# Revit family: Rohrschelle Maxima PSM, M10-M12, Ø 84-129, o.D
name_source: partatom
category: HLS-Bauteile
revit_build: Autodesk Revit 2017 (Build: 20190507_1515(x64)
units: mm (PartAtom-declared; Revit-internal decimal feet)

## family parameters
Arbeitsebenenbasiert = Ja
Beim Laden mit Abzugskörper schneiden = Nein
Bemaßung runder Anschluss = Durchmesser verwenden
Gemeinsam genutzt = Ja
Immer vertikal = Nein
Raumberechnungspunkt = Nein
Teiletyp = Normal

## types (6) — shared parameters
A = 25 mm  [stored 0.082021 ft]
Anschluss = M10/M12
Anschlußhöhe = 24 mm
Bauart = zweiteilig
Brandschutz = RAL-GZ 656
DF1 = 26 mm
DF2 = 28 mm  [stored 0.0918635 ft]
DVS = 15 mm  [stored 0.0492126 ft]
Fabrikat = MEFA
Firma = MEFA Befestigungs- und Montagesysteme GmbH
HGA = 22 mm  [stored 0.0721785 ft]
Kurztext1 = Rohrschelle Maxima PSM 30x3,0
MB = 30 mm  [stored 0.0984252 ft]
MD = 3 mm  [stored 0.00984252 ft]
Material = Stahl
Materialmaße = 30x3,0 mm
Materialname = S235
Mengeneinheit = St
Oberflaeche = galvanisch verzinkt
Verschluss = Pendelsteckmuttern
Verschluss-Schraube = M8
Vorgabe-Ansicht = 1219 mm
max. zul. Last = 4.00 kN
max. zul. Last horizontal = 0.00 kN
max. zul. Last vertikal = 0.00 kN
vpe = 1 St
zero-valued in all types: Nennweite DN Rohr, Rohraußendurchmesser, Stärke Material

## per-type parameters (varying)
| type | AB | Achsabstand | Artikelnummer | B | Breite | D | Dmax | Dmin | EAN | Gewicht | Gewicht pro Bauteil | H | Kurztext2 | R | RM | Rohraußendurchmesser Zoll | S | max. Höhe | max. Rohraußendurchmesser | min. Rohraußendurchmesser |
| Maxima PSM, M10/M12, Ø 84- 90, o.D. | 6 mm  [stored 0.019685 ft] | 124 mm | 008809301 | 150 mm | 150 mm | 90 mm  [stored 0.295276 ft] | 90 mm  [stored 0.295276 ft] | 84 mm  [stored 0.275591 ft] | 4250928455062 | 0.35 kg | 0.35 kg | 118 mm  [stored 0.387139 ft] | 84 - 90 mm M10/M12 | 45 mm  [stored 0.147638 ft] | 48 mm  [stored 0.15748 ft] | 3 Zoll | 124 mm  [stored 0.406824 ft] | 119 mm  [stored 0.39042 ft] | 90 mm  [stored 0.295276 ft] | 84 mm  [stored 0.275591 ft] |
| Maxima PSM, M10/M12, Ø 96-102, o.D. | 6 mm  [stored 0.019685 ft] | 136 mm | 008810501 | 162 mm | 162 mm | 102 mm | 102 mm | 96 mm  [stored 0.314961 ft] | 4250928455079 | 0.37 kg | 0.37 kg | 130 mm  [stored 0.426509 ft] | 96 - 102 mm M10/M12 | 51 mm | 54 mm | Zoll | 136 mm | 129 mm  [stored 0.423228 ft] | 102 mm | 96 mm  [stored 0.314961 ft] |
| Maxima PSM, M10/M12, Ø106-112, o.D. | 6 mm  [stored 0.019685 ft] | 146 mm | 008811301 | 172 mm | 172 mm | 112 mm  [stored 0.367454 ft] | 112 mm  [stored 0.367454 ft] | 106 mm  [stored 0.347769 ft] | 4250928455086 | 0.40 kg | 0.40 kg | 140 mm  [stored 0.459318 ft] | 106 - 112 mm M10/M12 | 56 mm  [stored 0.183727 ft] | 59 mm | Zoll | 146 mm  [stored 0.479003 ft] | 139 mm  [stored 0.456037 ft] | 112 mm  [stored 0.367454 ft] | 106 mm  [stored 0.347769 ft] |
| Maxima PSM, M10/M12, Ø114-118, o.D. | 4 mm  [stored 0.0131234 ft] | 152 mm | 008811901 | 178 mm | 178 mm | 118 mm  [stored 0.387139 ft] | 118 mm  [stored 0.387139 ft] | 114 mm  [stored 0.374016 ft] | 4250928455093 | 0.42 kg | 0.42 kg | 146 mm  [stored 0.479003 ft] | 114 - 118 mm M10/M12 | 59 mm | 62 mm  [stored 0.203412 ft] | 4 Zoll | 152 mm | 145 mm  [stored 0.475722 ft] | 118 mm  [stored 0.387139 ft] | 114 mm  [stored 0.374016 ft] |
| Maxima PSM, M10/M12, Ø120-124, o.D. | 4 mm  [stored 0.0131234 ft] | 158 mm | 008812501 | 184 mm | 184 mm | 124 mm  [stored 0.406824 ft] | 124 mm  [stored 0.406824 ft] | 120 mm  [stored 0.393701 ft] | 4250928455147 | 0.43 kg | 0.43 kg | 152 mm | 120 - 124 mm M10/M12 | 62 mm  [stored 0.203412 ft] | 65 mm  [stored 0.213255 ft] | Zoll | 158 mm | 151 mm  [stored 0.495407 ft] | 124 mm  [stored 0.406824 ft] | 120 mm  [stored 0.393701 ft] |
| Maxima PSM, M10/M12, Ø125-129, o.D. | 4 mm  [stored 0.0131234 ft] | 163 mm | 008813001 | 189 mm | 189 mm | 129 mm  [stored 0.423228 ft] | 129 mm  [stored 0.423228 ft] | 125 mm  [stored 0.410105 ft] | 4250928455109 | 0.44 kg | 0.44 kg | 157 mm | 125 - 129 mm M10/M12 | 65 mm  [stored 0.213255 ft] | 68 mm | Zoll | 163 mm | 156 mm | 129 mm  [stored 0.423228 ft] | 125 mm  [stored 0.410105 ft] |

note: [stored X ft] marks values corroborated as IEEE doubles in the binary element streams (Revit-internal decimal feet)

## geometry (parser evidence)
native form markers: Sweep x2
no freeform markers — native parametric forms only
